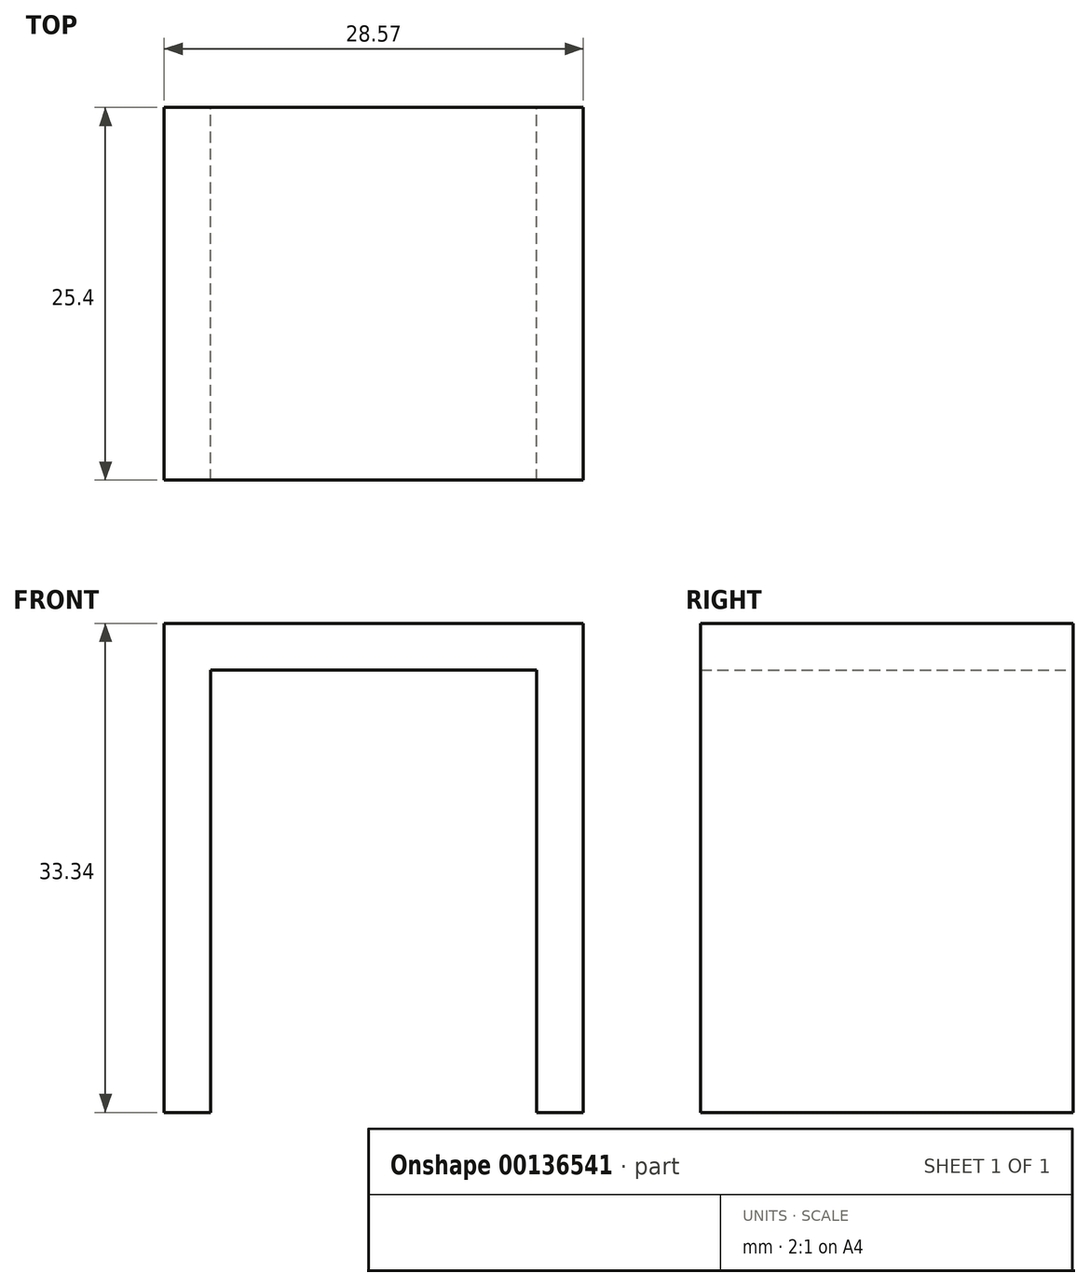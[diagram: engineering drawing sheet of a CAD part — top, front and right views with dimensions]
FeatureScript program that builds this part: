
annotation { "Feature Type Name" : "Feature", "Feature Type Description" : "" }
export const myFeature = defineFeature(function(context is Context, id is Id, definition is map)
    precondition{}
    {
        {
            var Q0;
            Q0=qCreatedBy(makeId("Front.planeOp"),FACE);
            var sketch = newSketch(context, id + "F0", { "sketchPlane" : qUnion([Q0])});
            skLineSegment(sketch, "E0.bottom", {"start": v(0, 0) * mm, "end": v(3.18, 0) * mm});
            skLineSegment(sketch, "E0.top", {"start": v(0, 33.34) * mm, "end": v(28.57, 33.34) * mm});
            skLineSegment(sketch, "E0.left", {"start": v(0, 0) * mm, "end": v(0, 33.34) * mm});
            skLineSegment(sketch, "E0.right", {"start": v(28.58, 0) * mm, "end": v(28.58, 33.34) * mm});
            skLineSegment(sketch, "E1.top", {"start": v(3.17, 30.16) * mm, "end": v(25.4, 30.16) * mm});
            skLineSegment(sketch, "E1.left", {"start": v(3.18, 0) * mm, "end": v(3.17, 30.16) * mm});
            skLineSegment(sketch, "E1.right", {"start": v(25.4, 0) * mm, "end": v(25.4, 30.16) * mm});
            skLineSegment(sketch, "E2.trimOffspring", {"start": v(25.4, 0) * mm, "end": v(28.58, 0) * mm});
            skSolve(sketch);
        }
        {
            var Q0;
            Q0 = qSketchRegion(id + "F0", true);
            extrude(context, id + "F1", {"entities" : qUnion([Q0]), "depth" : 25.4 * mm});
        }
    });
